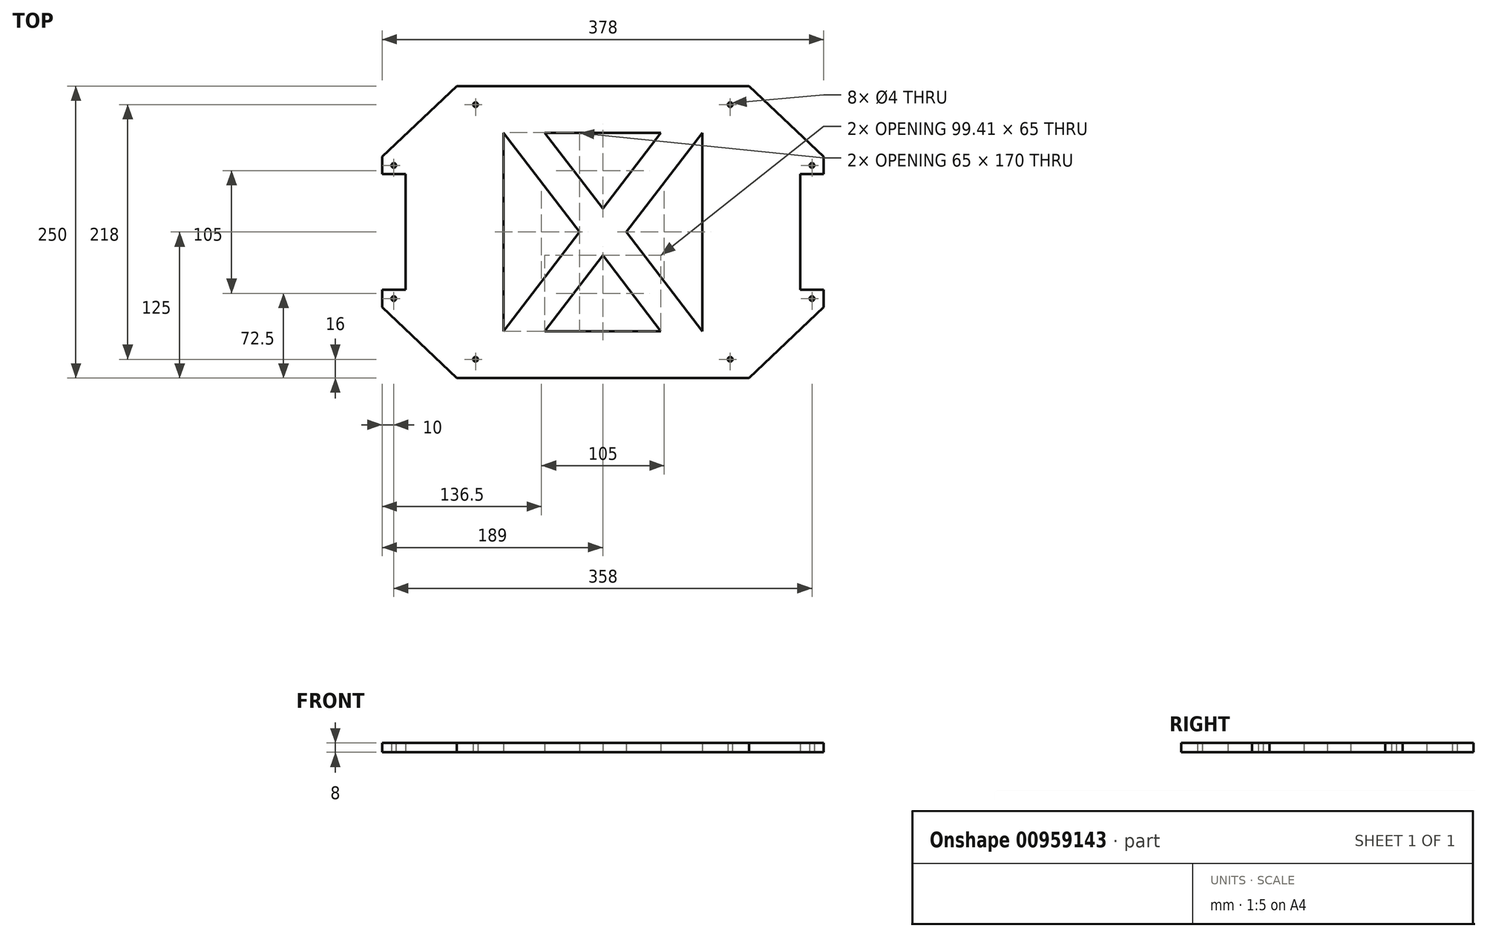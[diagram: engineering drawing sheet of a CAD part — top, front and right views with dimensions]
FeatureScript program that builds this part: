
annotation { "Feature Type Name" : "Feature", "Feature Type Description" : "" }
export const myFeature = defineFeature(function(context is Context, id is Id, definition is map)
    precondition{}
    {
        {
            var Q0;
            Q0=qCreatedBy(makeId("Top.planeOp"),FACE);
            var sketch = newSketch(context, id + "F0", { "sketchPlane" : qUnion([Q0])});
            skLineSegment(sketch, "E0.bottom", {"start": v(-125, 125) * mm, "end": v(125, 125) * mm});
            skLineSegment(sketch, "E0.top", {"start": v(-125, -125) * mm, "end": v(125, -125) * mm});
            skLineSegment(sketch, "E0.left", {"start": v(-125, 125) * mm, "end": v(-125, -125) * mm});
            skLineSegment(sketch, "E0.right", {"start": v(125, 125) * mm, "end": v(125, -125) * mm});
            skPoint(sketch, "E0.middle", {"position": v(0, 0) * mm});
            skLineSegment(sketch, "E1", {"start": v(0, 0) * mm, "end": v(-125, 0) * mm});
            skLineSegment(sketch, "E2.bottom", {"start": v(-125, 64.5) * mm, "end": v(-169, 64.5) * mm});
            skLineSegment(sketch, "E2.top", {"start": v(-125, -64.5) * mm, "end": v(-169, -64.5) * mm});
            skLineSegment(sketch, "E2.left", {"start": v(-125, 64.5) * mm, "end": v(-125, -64.5) * mm});
            skLineSegment(sketch, "E2.right", {"start": v(-169, 64.5) * mm, "end": v(-169, -64.5) * mm});
            skLineSegment(sketch, "E3.bottom", {"start": v(-169, 64.5) * mm, "end": v(-189, 64.5) * mm});
            skLineSegment(sketch, "E3.top", {"start": v(-169, 49.5) * mm, "end": v(-189, 49.5) * mm});
            skLineSegment(sketch, "E3.left", {"start": v(-169, 64.5) * mm, "end": v(-169, 49.5) * mm});
            skLineSegment(sketch, "E3.right", {"start": v(-189, 64.5) * mm, "end": v(-189, 49.5) * mm});
            skLineSegment(sketch, "E4.bottom", {"start": v(-169, -64.5) * mm, "end": v(-189, -64.5) * mm});
            skLineSegment(sketch, "E4.top", {"start": v(-169, -49.5) * mm, "end": v(-189, -49.5) * mm});
            skLineSegment(sketch, "E4.left", {"start": v(-169, -64.5) * mm, "end": v(-169, -49.5) * mm});
            skLineSegment(sketch, "E4.right", {"start": v(-189, -64.5) * mm, "end": v(-189, -49.5) * mm});
            skPoint(sketch, "E5", {"position": v(-179, 57) * mm});
            skPoint(sketch, "E6", {"position": v(-179, -57) * mm});
            skPoint(sketch, "E7", {"position": v(-169, 0) * mm});
            skLineSegment(sketch, "E8", {"start": v(-169, 0) * mm, "end": v(-125, 0) * mm});
            skPoint(sketch, "E9", {"position": v(125, 0) * mm});
            skLineSegment(sketch, "E10", {"start": v(0, 0) * mm, "end": v(125, 0) * mm});
            skPoint(sketch, "E11", {"position": v(0, 125) * mm});
            skLineSegment(sketch, "E12", {"start": v(0, 125) * mm, "end": v(0, 0) * mm});
            skLineSegment(sketch, "E13", {"start": v(0, 0) * mm, "end": v(0, -125) * mm});
            skLineSegment(sketch, "E14.MirrorCS", {"start": v(169, -64.5) * mm, "end": v(169, -49.5) * mm});
            skPoint(sketch, "E15.MirrorP", {"position": v(179, -57) * mm});
            skLineSegment(sketch, "E16.MirrorCS", {"start": v(169, 64.5) * mm, "end": v(169, 49.5) * mm});
            skLineSegment(sketch, "E17.MirrorCS", {"start": v(169, -64.5) * mm, "end": v(189, -64.5) * mm});
            skLineSegment(sketch, "E18.MirrorCS", {"start": v(189, -64.5) * mm, "end": v(189, -49.5) * mm});
            skLineSegment(sketch, "E19.MirrorCS", {"start": v(169, -49.5) * mm, "end": v(189, -49.5) * mm});
            skLineSegment(sketch, "E20.MirrorCS", {"start": v(169, 49.5) * mm, "end": v(189, 49.5) * mm});
            skLineSegment(sketch, "E21.MirrorCS", {"start": v(189, 64.5) * mm, "end": v(189, 49.5) * mm});
            skLineSegment(sketch, "E22.MirrorCS", {"start": v(125, 64.5) * mm, "end": v(125, -64.5) * mm});
            skLineSegment(sketch, "E23.MirrorCS", {"start": v(169, 64.5) * mm, "end": v(169, -64.5) * mm});
            skLineSegment(sketch, "E24.MirrorCS", {"start": v(125, 125) * mm, "end": v(-125, 125) * mm});
            skLineSegment(sketch, "E25.MirrorCS", {"start": v(169, 0) * mm, "end": v(125, 0) * mm});
            skLineSegment(sketch, "E26.MirrorCS", {"start": v(125, 64.5) * mm, "end": v(169, 64.5) * mm});
            skPoint(sketch, "E27.MirrorP", {"position": v(179, 57) * mm});
            skPoint(sketch, "E28.MirrorP", {"position": v(169, 0) * mm});
            skLineSegment(sketch, "E29.MirrorCS", {"start": v(125, -125) * mm, "end": v(-125, -125) * mm});
            skLineSegment(sketch, "E30.MirrorCS", {"start": v(125, -64.5) * mm, "end": v(169, -64.5) * mm});
            skLineSegment(sketch, "E31.MirrorCS", {"start": v(169, 64.5) * mm, "end": v(189, 64.5) * mm});
            skCircle(sketch, "E32", {"center": v(-179, 57) * mm, "radius": 2 * mm});
            skCircle(sketch, "E33", {"center": v(-179, -57) * mm, "radius": 2 * mm});
            skCircle(sketch, "E34.MirrorC", {"center": v(179, 57) * mm, "radius": 2 * mm});
            skCircle(sketch, "E35.MirrorC", {"center": v(179, -57) * mm, "radius": 2 * mm});
            skPoint(sketch, "E36", {"position": v(-109, 109) * mm});
            skPoint(sketch, "E37", {"position": v(-109, -109) * mm});
            skPoint(sketch, "E38.MirrorP", {"position": v(109, 109) * mm});
            skPoint(sketch, "E39.MirrorP", {"position": v(109, -109) * mm});
            skCircle(sketch, "E40", {"center": v(-109, 109) * mm, "radius": 2 * mm});
            skCircle(sketch, "E41", {"center": v(-109, -109) * mm, "radius": 2 * mm});
            skCircle(sketch, "E42.MirrorC", {"center": v(109, -109) * mm, "radius": 2 * mm});
            skCircle(sketch, "E43.MirrorC", {"center": v(109, 109) * mm, "radius": 2 * mm});
            skLineSegment(sketch, "E44", {"start": v(-20, 0) * mm, "end": v(-85, 85) * mm});
            skLineSegment(sketch, "E45", {"start": v(-85, 85) * mm, "end": v(-85, 0) * mm});
            skLineSegment(sketch, "E46.MirrorCS", {"start": v(-20, 0) * mm, "end": v(-85, -85) * mm});
            skLineSegment(sketch, "E47.MirrorCS", {"start": v(-85, -85) * mm, "end": v(-85, 0) * mm});
            skLineSegment(sketch, "E48.MirrorCS", {"start": v(20, 0) * mm, "end": v(85, 85) * mm});
            skLineSegment(sketch, "E49.MirrorCS", {"start": v(85, 85) * mm, "end": v(85, 0) * mm});
            skLineSegment(sketch, "E50.MirrorCS", {"start": v(20, 0) * mm, "end": v(85, -85) * mm});
            skLineSegment(sketch, "E51.MirrorCS", {"start": v(85, -85) * mm, "end": v(85, 0) * mm});
            skPoint(sketch, "E52", {"position": v(0, 20) * mm});
            skLineSegment(sketch, "E53", {"start": v(0, 20) * mm, "end": v(-49.7, 85) * mm});
            skLineSegment(sketch, "E54", {"start": v(-49.7, 85) * mm, "end": v(0, 85) * mm});
            skLineSegment(sketch, "E55.MirrorCS", {"start": v(49.7, 85) * mm, "end": v(0, 85) * mm});
            skLineSegment(sketch, "E56.MirrorCS", {"start": v(0, 20) * mm, "end": v(49.7, 85) * mm});
            skLineSegment(sketch, "E57.MirrorCS", {"start": v(0, -20) * mm, "end": v(-49.7, -85) * mm});
            skLineSegment(sketch, "E58.MirrorCS", {"start": v(0, -20) * mm, "end": v(49.7, -85) * mm});
            skLineSegment(sketch, "E59.MirrorCS", {"start": v(49.7, -85) * mm, "end": v(0, -85) * mm});
            skLineSegment(sketch, "E60.MirrorCS", {"start": v(-49.7, -85) * mm, "end": v(0, -85) * mm});
            skLineSegment(sketch, "E61", {"start": v(-189, 64.5) * mm, "end": v(-125, 125) * mm});
            skLineSegment(sketch, "E62.MirrorCS", {"start": v(189, 64.5) * mm, "end": v(125, 125) * mm});
            skLineSegment(sketch, "E63.MirrorCS", {"start": v(-189, -64.5) * mm, "end": v(-125, -125) * mm});
            skLineSegment(sketch, "E64.MirrorCS", {"start": v(189, -64.5) * mm, "end": v(125, -125) * mm});
            skSolve(sketch);
        }
        {
            var Q0;
            Q0=makeQuery(id+"F0.imprint","IMPRINT",FACE,{"disambiguationData":[TD([[makeQuery(id+"F0.imprint","IMPRINT",EDGE,{"derivedFrom":sQuery(id+"F0.wireOp",EDGE,"E3.bottom")}),1.0]])]});
            var Q1;
            Q1=makeQuery(id+"F0.imprint","IMPRINT",FACE,{"disambiguationData":[TD([[makeQuery(id+"F0.imprint","IMPRINT",EDGE,{"derivedFrom":sQuery(id+"F0.wireOp",EDGE,"E4.bottom")}),-1.0]])]});
            var Q2;
            {var subQ1=sQuery(id+"F0.wireOp",EDGE,"E1");Q2=makeQuery(id+"F0.imprint","IMPRINT",FACE,{"disambiguationData":[TD([[makeQuery(id+"F0.imprint","IMPRINT",EDGE,{"derivedFrom":subQ1}),-1.0]])]});}
            var Q3;
            {var subQ0=sQuery(id+"F0.wireOp",EDGE,"E1");Q3=makeQuery(id+"F0.imprint","IMPRINT",FACE,{"disambiguationData":[TD([[makeQuery(id+"F0.imprint","IMPRINT",EDGE,{"derivedFrom":subQ0}),1.0]])]});}
            var Q4;
            {var subQ4=sQuery(id+"F0.wireOp",EDGE,"E2.bottom");Q4=makeQuery(id+"F0.imprint","IMPRINT",FACE,{"disambiguationData":[TD([[makeQuery(id+"F0.imprint","IMPRINT",EDGE,{"derivedFrom":subQ4}),1.0]])]});}
            var Q5;
            {var subQ1=sQuery(id+"F0.wireOp",EDGE,"E2.top");Q5=makeQuery(id+"F0.imprint","IMPRINT",FACE,{"disambiguationData":[TD([[makeQuery(id+"F0.imprint","IMPRINT",EDGE,{"derivedFrom":subQ1}),-1.0]])]});}
            var Q6;
            {var subQ4=sQuery(id+"F0.wireOp",EDGE,"E12");Q6=makeQuery(id+"F0.imprint","IMPRINT",FACE,{"disambiguationData":[TD([[makeQuery(id+"F0.imprint","IMPRINT",EDGE,{"derivedFrom":subQ4}),1.0]])]});}
            var Q7;
            {var subQ4=sQuery(id+"F0.wireOp",EDGE,"E13");Q7=makeQuery(id+"F0.imprint","IMPRINT",FACE,{"disambiguationData":[TD([[makeQuery(id+"F0.imprint","IMPRINT",EDGE,{"derivedFrom":subQ4}),1.0]])]});}
            var Q8;
            {var subQ1=sQuery(id+"F0.wireOp",EDGE,"E25.MirrorCS");Q8=makeQuery(id+"F0.imprint","IMPRINT",FACE,{"disambiguationData":[TD([[makeQuery(id+"F0.imprint","IMPRINT",EDGE,{"derivedFrom":subQ1}),1.0]])]});}
            var Q9;
            {var subQ1=sQuery(id+"F0.wireOp",EDGE,"E25.MirrorCS");Q9=makeQuery(id+"F0.imprint","IMPRINT",FACE,{"disambiguationData":[TD([[makeQuery(id+"F0.imprint","IMPRINT",EDGE,{"derivedFrom":subQ1}),-1.0]])]});}
            var Q10;
            {var subQ0=sQuery(id+"F0.wireOp",EDGE,"E20.MirrorCS");Q10=makeQuery(id+"F0.imprint","IMPRINT",FACE,{"disambiguationData":[TD([[makeQuery(id+"F0.imprint","IMPRINT",EDGE,{"derivedFrom":subQ0}),1.0]])]});}
            var Q11;
            {var subQ0=sQuery(id+"F0.wireOp",EDGE,"E17.MirrorCS");Q11=makeQuery(id+"F0.imprint","IMPRINT",FACE,{"disambiguationData":[TD([[makeQuery(id+"F0.imprint","IMPRINT",EDGE,{"derivedFrom":subQ0}),1.0]])]});}
            var Q12;
            {var subQ2=sQuery(id+"F0.wireOp",EDGE,"E2.bottom");Q12=makeQuery(id+"F0.imprint","IMPRINT",FACE,{"disambiguationData":[TD([[makeQuery(id+"F0.imprint","IMPRINT",EDGE,{"derivedFrom":subQ2}),-1.0]])]});}
            var Q13;
            {var subQ2=sQuery(id+"F0.wireOp",EDGE,"E2.top");Q13=makeQuery(id+"F0.imprint","IMPRINT",FACE,{"disambiguationData":[TD([[makeQuery(id+"F0.imprint","IMPRINT",EDGE,{"derivedFrom":subQ2}),1.0]])]});}
            var Q14;
            {var subQ0=sQuery(id+"F0.wireOp",EDGE,"E26.MirrorCS");Q14=makeQuery(id+"F0.imprint","IMPRINT",FACE,{"disambiguationData":[TD([[makeQuery(id+"F0.imprint","IMPRINT",EDGE,{"derivedFrom":subQ0}),1.0]])]});}
            var Q15;
            {var subQ0=sQuery(id+"F0.wireOp",EDGE,"E30.MirrorCS");Q15=makeQuery(id+"F0.imprint","IMPRINT",FACE,{"disambiguationData":[TD([[makeQuery(id+"F0.imprint","IMPRINT",EDGE,{"derivedFrom":subQ0}),-1.0]])]});}
            extrude(context, id + "F1", {"entities" : qUnion([Q0, Q1, Q2, Q3, Q4, Q5, Q6, Q7, Q8, Q9, Q10, Q11, Q12, Q13, Q14, Q15]), "endBound" : BoundingType.SYMMETRIC, "depth" : 8 * mm, "offsetDistance" : 25.4 * mm});
        }
    });
